# Revit family: 0043426
name_source: partatom
category: Lighting Fixtures
revit_build: Autodesk Revit 2017 (Build: 20190507_1515(x64)
units: mm (PartAtom-declared; Revit-internal decimal feet)

## family parameters
Cut with Voids When Loaded = No
Host = Face
Light Source = Yes
OmniClass Number = 23.80.70.00
OmniClass Title = Lighting
Part Type = Normal
Room Calculation Point = No
Round Connector Dimension = Use Diameter
Shared = No

## types (16) — shared parameters
Assembly Code = D5020200
AssetType = Fixed
ClassificationName = Uniclass2015
ClassificationValue = EF_70_80
Color Filter = 16777215
Default Elevation = 1219 mm
Dimming Lamp Color Temperature Shift = <None>
DocumentationLiterature = http://www.sylvania-lighting.com
ElectricShockClassification = Class I
Emit Shape Visible in Rendering = No
Emit from Circle Diameter = 610 mm
IfcExportAs = IfcLightFixtureType
IfcExportType = IfcLightFixtureType
ImpactProtectionIndex = IK03
IngressProtection = IP44
Keynote = 16500
Lamp = LED
LampColourRenderingIndex = 80
LampMacAdamStep = 6
LampsType = LED
Manufacturer = Feilo Sylvania
ManufacturerName = Feilo Sylvania
Material = steel housing, other diffuser
Material_1_SYL = <By Category>
Material_2_SYL = <By Category>
Material_3_SYL = <By Category>
Material_4_SYL = <By Category>
SENSOR_SYL = 12 mm  [stored 0.0393701 ft]
Tilt Angle = -90.00°
Type Image = <None>
URL = http://www.sylvania-lighting.com
Voltage = 0 V
YIN_SENSOR_SYL = No
zero-valued in all types: Cost

## per-type parameters (varying)
- 0043436_3000K START eco Surface IP44 2050LM MW 830/840 DT: Apparent Load=0 VA; BOTTOM_HEIGHT_SYL=85 mm  [stored 0.278871 ft]; BOTTOM_R_SYL=150 mm; LUM_H_SYL=100 mm  [stored 0.328084 ft]; LUM_R_HEIGHT_SYL=70 mm; LUM_R_SYL=180 mm  [stored 0.590551 ft]; LampColourTemperature=3000 K; LampNominalLuminous=2050 lm; Model=Start eco Surface IP44 2050lm MW 830/840 DualTone; ModelNumber=0043436; ModelReference=Start eco Surface IP44 2050lm MW 830/840 DualTone; Name=Start eco Surface IP44 2050lm MW 830/840 DualTone; NominalDepth=360 mm  [stored 1.1811 ft]; NominalHeight=100 mm  [stored 0.328084 ft]; NominalLength=360 mm  [stored 1.1811 ft]; Photometric Web File=0043436_3000K.ies; PowerFactor=0; TypeName=Start eco Surface IP44 2050lm MW 830/840 DualTone; Weight=3.42 kg; YIN_180_SYL=No; YIN_250_SYL=No; YIN_330_SYL=No; YIN_360_SYL=Yes
- 0043435_4000K START eco Surface IP44 1550LM MW 830/840 DT: Apparent Load=0 VA; BOTTOM_HEIGHT_SYL=81 mm  [stored 0.265748 ft]; BOTTOM_R_SYL=150 mm; LUM_H_SYL=96 mm  [stored 0.314961 ft]; LUM_R_HEIGHT_SYL=66 mm  [stored 0.216535 ft]; LUM_R_SYL=165 mm; LampColourTemperature=4000 K; LampNominalLuminous=1550 lm; Model=Start eco Surface IP44 1550lm MW 830/840 DualTone; ModelNumber=0043435; ModelReference=Start eco Surface IP44 1550lm MW 830/840 DualTone; Name=Start eco Surface IP44 1550lm MW 830/840 DualTone; NominalDepth=330 mm; NominalHeight=96 mm  [stored 0.314961 ft]; NominalLength=330 mm; Photometric Web File=0043435_4000K.ies; PowerFactor=0; TypeName=Start eco Surface IP44 1550lm MW 830/840 DualTone; Weight=3.42 kg; YIN_180_SYL=No; YIN_250_SYL=No; YIN_330_SYL=Yes; YIN_360_SYL=No
- 0043435_3000K START eco Surface IP44 1550LM MW 830/840 DT: Apparent Load=0 VA; BOTTOM_HEIGHT_SYL=81 mm  [stored 0.265748 ft]; BOTTOM_R_SYL=150 mm; LUM_H_SYL=96 mm  [stored 0.314961 ft]; LUM_R_HEIGHT_SYL=66 mm  [stored 0.216535 ft]; LUM_R_SYL=165 mm; LampColourTemperature=3000 K; LampNominalLuminous=1550 lm; Model=Start eco Surface IP44 1550lm MW 830/840 DualTone; ModelNumber=0043435; ModelReference=Start eco Surface IP44 1550lm MW 830/840 DualTone; Name=Start eco Surface IP44 1550lm MW 830/840 DualTone; NominalDepth=330 mm; NominalHeight=96 mm  [stored 0.314961 ft]; NominalLength=330 mm; Photometric Web File=0043435_3000K.ies; PowerFactor=0; TypeName=Start eco Surface IP44 1550lm MW 830/840 DualTone; Weight=3.42 kg; YIN_180_SYL=No; YIN_250_SYL=No; YIN_330_SYL=Yes; YIN_360_SYL=No
- 0043434_4000K START eco Surface IP44 2050LM DIM 30/840 DT: Apparent Load=0 VA; BOTTOM_HEIGHT_SYL=85 mm  [stored 0.278871 ft]; BOTTOM_R_SYL=150 mm; LUM_H_SYL=100 mm  [stored 0.328084 ft]; LUM_R_HEIGHT_SYL=70 mm; LUM_R_SYL=180 mm  [stored 0.590551 ft]; LampColourTemperature=4000 K; LampNominalLuminous=2050 lm; Model=Start eco Surface IP44 2050lm DIM 830/840 DualTone; ModelNumber=0043434; ModelReference=Start eco Surface IP44 2050lm DIM 830/840 DualTone; Name=Start eco Surface IP44 2050lm DIM 830/840 DualTone; NominalDepth=360 mm  [stored 1.1811 ft]; NominalHeight=100 mm  [stored 0.328084 ft]; NominalLength=360 mm  [stored 1.1811 ft]; Photometric Web File=0043434_4000K.ies; PowerFactor=0; TypeName=Start eco Surface IP44 2050lm DIM 830/840 DualTone; Weight=3.54 kg; YIN_180_SYL=No; YIN_250_SYL=No; YIN_330_SYL=No; YIN_360_SYL=Yes
- 0043434_3000K START eco Surface IP44 2050LM DIM 30/840 DT: Apparent Load=0 VA; BOTTOM_HEIGHT_SYL=85 mm  [stored 0.278871 ft]; BOTTOM_R_SYL=150 mm; LUM_H_SYL=100 mm  [stored 0.328084 ft]; LUM_R_HEIGHT_SYL=70 mm; LUM_R_SYL=180 mm  [stored 0.590551 ft]; LampColourTemperature=3000 K; LampNominalLuminous=2050 lm; Model=Start eco Surface IP44 2050lm DIM 830/840 DualTone; ModelNumber=0043434; ModelReference=Start eco Surface IP44 2050lm DIM 830/840 DualTone; Name=Start eco Surface IP44 2050lm DIM 830/840 DualTone; NominalDepth=360 mm  [stored 1.1811 ft]; NominalHeight=100 mm  [stored 0.328084 ft]; NominalLength=360 mm  [stored 1.1811 ft]; Photometric Web File=0043434_3000K.ies; PowerFactor=0; TypeName=Start eco Surface IP44 2050lm DIM 830/840 DualTone; Weight=3.54 kg; YIN_180_SYL=No; YIN_250_SYL=No; YIN_330_SYL=No; YIN_360_SYL=Yes
- 0043433_4000K START eco Surface IP44 1550LM DIM 830/840 DT: Apparent Load=0 VA; BOTTOM_HEIGHT_SYL=81 mm  [stored 0.265748 ft]; BOTTOM_R_SYL=150 mm; LUM_H_SYL=96 mm  [stored 0.314961 ft]; LUM_R_HEIGHT_SYL=66 mm  [stored 0.216535 ft]; LUM_R_SYL=165 mm; LampColourTemperature=4000 K; LampNominalLuminous=1550 lm; Model=Start eco Surface IP44 1550lm DIM 830/840 DualTone; ModelNumber=0043433; ModelReference=Start eco Surface IP44 1550lm DIM 830/840 DualTone; Name=Start eco Surface IP44 1550lm DIM 830/840 DualTone; NominalDepth=330 mm; NominalHeight=96 mm  [stored 0.314961 ft]; NominalLength=330 mm; Photometric Web File=0043433_4000K.ies; PowerFactor=0; TypeName=Start eco Surface IP44 1550lm DIM 830/840 DualTone; Weight=3.54 kg; YIN_180_SYL=No; YIN_250_SYL=No; YIN_330_SYL=Yes; YIN_360_SYL=No
- 0043433_3000K START eco Surface IP44 1550LM DIM 830/840 DT: Apparent Load=0 VA; BOTTOM_HEIGHT_SYL=81 mm  [stored 0.265748 ft]; BOTTOM_R_SYL=150 mm; LUM_H_SYL=96 mm  [stored 0.314961 ft]; LUM_R_HEIGHT_SYL=66 mm  [stored 0.216535 ft]; LUM_R_SYL=165 mm; LampColourTemperature=3000 K; LampNominalLuminous=1550 lm; Model=Start eco Surface IP44 1550lm DIM 830/840 DualTone; ModelNumber=0043433; ModelReference=Start eco Surface IP44 1550lm DIM 830/840 DualTone; Name=Start eco Surface IP44 1550lm DIM 830/840 DualTone; NominalDepth=330 mm; NominalHeight=96 mm  [stored 0.314961 ft]; NominalLength=330 mm; Photometric Web File=0043433_3000K.ies; PowerFactor=0; TypeName=Start eco Surface IP44 1550lm DIM 830/840 DualTone; Weight=3.54 kg; YIN_180_SYL=No; YIN_250_SYL=No; YIN_330_SYL=Yes; YIN_360_SYL=No
- 0043428_4000K START eco Surface IP44 2050LM 830/840 DT: Apparent Load=0 VA; BOTTOM_HEIGHT_SYL=85 mm  [stored 0.278871 ft]; BOTTOM_R_SYL=150 mm; LUM_H_SYL=100 mm  [stored 0.328084 ft]; LUM_R_HEIGHT_SYL=70 mm; LUM_R_SYL=180 mm  [stored 0.590551 ft]; LampColourTemperature=4000 K; LampNominalLuminous=2050 lm; Model=Start eco Surface IP44 2050lm 830/840 DualTone; ModelNumber=0043428; ModelReference=Start eco Surface IP44 2050lm 830/840 DualTone; Name=Start eco Surface IP44 2050lm 830/840 DualTone; NominalDepth=360 mm  [stored 1.1811 ft]; NominalHeight=100 mm  [stored 0.328084 ft]; NominalLength=360 mm  [stored 1.1811 ft]; Photometric Web File=0043428_4000K.ies; PowerFactor=0; TypeName=Start eco Surface IP44 2050lm 830/840 DualTone; Weight=3.12 kg; YIN_180_SYL=No; YIN_250_SYL=No; YIN_330_SYL=No; YIN_360_SYL=Yes
- 0043428_3000K START eco Surface IP44 2050LM 830/840 DT: Apparent Load=0 VA; BOTTOM_HEIGHT_SYL=85 mm  [stored 0.278871 ft]; BOTTOM_R_SYL=150 mm; LUM_H_SYL=100 mm  [stored 0.328084 ft]; LUM_R_HEIGHT_SYL=70 mm; LUM_R_SYL=180 mm  [stored 0.590551 ft]; LampColourTemperature=3000 K; LampNominalLuminous=2050 lm; Model=Start eco Surface IP44 2050lm 830/840 DualTone; ModelNumber=0043428; ModelReference=Start eco Surface IP44 2050lm 830/840 DualTone; Name=Start eco Surface IP44 2050lm 830/840 DualTone; NominalDepth=360 mm  [stored 1.1811 ft]; NominalHeight=100 mm  [stored 0.328084 ft]; NominalLength=360 mm  [stored 1.1811 ft]; Photometric Web File=0043428_3000K.ies; PowerFactor=0; TypeName=Start eco Surface IP44 2050lm 830/840 DualTone; Weight=3.12 kg; YIN_180_SYL=No; YIN_250_SYL=No; YIN_330_SYL=No; YIN_360_SYL=Yes
- 0043427_4000K START eco Surface IP44 1550LM 830/840 DT: Apparent Load=0 VA; BOTTOM_HEIGHT_SYL=81 mm  [stored 0.265748 ft]; BOTTOM_R_SYL=150 mm; LUM_H_SYL=96 mm  [stored 0.314961 ft]; LUM_R_HEIGHT_SYL=66 mm  [stored 0.216535 ft]; LUM_R_SYL=165 mm; LampColourTemperature=4000 K; LampNominalLuminous=1550 lm; Model=Start eco Surface IP44 1550lm 830/840 DualTone; ModelNumber=0043427; ModelReference=Start eco Surface IP44 1550lm 830/840 DualTone; Name=Start eco Surface IP44 1550lm 830/840 DualTone; NominalDepth=330 mm; NominalHeight=96 mm  [stored 0.314961 ft]; NominalLength=330 mm; Photometric Web File=0043427_4000K.ies; PowerFactor=0; TypeName=Start eco Surface IP44 1550lm 830/840 DualTone; Weight=3.12 kg; YIN_180_SYL=No; YIN_250_SYL=No; YIN_330_SYL=Yes; YIN_360_SYL=No
- 0043427_3000K START eco Surface IP44 1550LM 830/840 DT: Apparent Load=0 VA; BOTTOM_HEIGHT_SYL=81 mm  [stored 0.265748 ft]; BOTTOM_R_SYL=150 mm; LUM_H_SYL=96 mm  [stored 0.314961 ft]; LUM_R_HEIGHT_SYL=66 mm  [stored 0.216535 ft]; LUM_R_SYL=165 mm; LampColourTemperature=3000 K; LampNominalLuminous=1550 lm; Model=Start eco Surface IP44 1550lm 830/840 DualTone; ModelNumber=0043427; ModelReference=Start eco Surface IP44 1550lm 830/840 DualTone; Name=Start eco Surface IP44 1550lm 830/840 DualTone; NominalDepth=330 mm; NominalHeight=96 mm  [stored 0.314961 ft]; NominalLength=330 mm; Photometric Web File=0043427_3000K.ies; PowerFactor=0; TypeName=Start eco Surface IP44 1550lm 830/840 DualTone; Weight=3.12 kg; YIN_180_SYL=No; YIN_250_SYL=No; YIN_330_SYL=Yes; YIN_360_SYL=No
- 0043426_4000K START eco Surface IP44 1025LM 830/840 DT: Apparent Load=0 VA; BOTTOM_HEIGHT_SYL=65 mm  [stored 0.213255 ft]; BOTTOM_R_SYL=110 mm  [stored 0.360892 ft]; LUM_H_SYL=80 mm  [stored 0.262467 ft]; LUM_R_HEIGHT_SYL=50 mm  [stored 0.164042 ft]; LUM_R_SYL=125 mm  [stored 0.410105 ft]; LampColourTemperature=4000 K; LampNominalLuminous=1025 lm; Model=Start eco Surface IP44 1025lm 830/840 DualTone; ModelNumber=0043426; ModelReference=Start eco Surface IP44 1025lm 830/840 DualTone; Name=Start eco Surface IP44 1025lm 830/840 DualTone; NominalDepth=250 mm  [stored 0.82021 ft]; NominalHeight=80 mm  [stored 0.262467 ft]; NominalLength=250 mm  [stored 0.82021 ft]; Photometric Web File=0043426_4000K.ies; PowerFactor=0; TypeName=Start eco Surface IP44 1025lm 830/840 DualTone; Weight=1.5 kg; YIN_180_SYL=No; YIN_250_SYL=Yes; YIN_330_SYL=No; YIN_360_SYL=No
- 0043426_3000K START eco Surface IP44 1025LM 830/840 DT: Apparent Load=0 VA; BOTTOM_HEIGHT_SYL=65 mm  [stored 0.213255 ft]; BOTTOM_R_SYL=110 mm  [stored 0.360892 ft]; LUM_H_SYL=80 mm  [stored 0.262467 ft]; LUM_R_HEIGHT_SYL=50 mm  [stored 0.164042 ft]; LUM_R_SYL=125 mm  [stored 0.410105 ft]; LampColourTemperature=3000 K; LampNominalLuminous=1025 lm; Model=Start eco Surface IP44 1025lm 830/840 DualTone; ModelNumber=0043426; ModelReference=Start eco Surface IP44 1025lm 830/840 DualTone; Name=Start eco Surface IP44 1025lm 830/840 DualTone; NominalDepth=250 mm  [stored 0.82021 ft]; NominalHeight=80 mm  [stored 0.262467 ft]; NominalLength=250 mm  [stored 0.82021 ft]; Photometric Web File=0043426_3000K.ies; PowerFactor=0; TypeName=Start eco Surface IP44 1025lm 830/840 DualTone; Weight=1.5 kg; YIN_180_SYL=No; YIN_250_SYL=Yes; YIN_330_SYL=No; YIN_360_SYL=No
- 0043425_4000K START eco Surface IP44 520LM 830/840 DT: Apparent Load=6 VA; BOTTOM_HEIGHT_SYL=60 mm; BOTTOM_R_SYL=76 mm  [stored 0.249344 ft]; LUM_H_SYL=75 mm; LUM_R_HEIGHT_SYL=45 mm; LUM_R_SYL=90 mm  [stored 0.295276 ft]; LampColourTemperature=4000 K; LampNominalLuminous=520 lm; LuminousEfficacy=85 lm/W; Model=Start eco Surface IP44 520lm 830/840 DualTone; ModelNumber=0043425; ModelReference=Start eco Surface IP44 520lm 830/840 DualTone; Name=Start eco Surface IP44 520lm 830/840 DualTone; NominalDepth=180 mm  [stored 0.590551 ft]; NominalHeight=75 mm; NominalLength=180 mm  [stored 0.590551 ft]; Photometric Web File=0043425_4000K.ies; PowerConsumption=6 W; PowerFactor=0.8; TypeName=Start eco Surface IP44 520lm 830/840 DualTone; Weight=1.02 kg; YIN_180_SYL=Yes; YIN_250_SYL=No; YIN_330_SYL=No; YIN_360_SYL=No
- 0043425_3000K START eco Surface IP44 520LM 830/840 DT: Apparent Load=6 VA; BOTTOM_HEIGHT_SYL=60 mm; BOTTOM_R_SYL=76 mm  [stored 0.249344 ft]; LUM_H_SYL=75 mm; LUM_R_HEIGHT_SYL=45 mm; LUM_R_SYL=90 mm  [stored 0.295276 ft]; LampColourTemperature=3000 K; LampNominalLuminous=520 lm; LuminousEfficacy=85 lm/W; Model=Start eco Surface IP44 520lm 830/840 DualTone; ModelNumber=0043425; ModelReference=Start eco Surface IP44 520lm 830/840 DualTone; Name=Start eco Surface IP44 520lm 830/840 DualTone; NominalDepth=180 mm  [stored 0.590551 ft]; NominalHeight=75 mm; NominalLength=180 mm  [stored 0.590551 ft]; Photometric Web File=0043425_3000K.ies; PowerConsumption=6 W; PowerFactor=0.8; TypeName=Start eco Surface IP44 520lm 830/840 DualTone; Weight=1.02 kg; YIN_180_SYL=Yes; YIN_250_SYL=No; YIN_330_SYL=No; YIN_360_SYL=No
- 0043436_4000K START eco Surface IP44 2050LM MW 830/840 DT: Apparent Load=0 VA; BOTTOM_HEIGHT_SYL=85 mm  [stored 0.278871 ft]; BOTTOM_R_SYL=150 mm; LUM_H_SYL=100 mm  [stored 0.328084 ft]; LUM_R_HEIGHT_SYL=70 mm; LUM_R_SYL=180 mm  [stored 0.590551 ft]; LampColourTemperature=4000 K; LampNominalLuminous=2050 lm; Model=Start eco Surface IP44 2050lm MW 830/840 DualTone; ModelNumber=0043436; ModelReference=Start eco Surface IP44 2050lm MW 830/840 DualTone; Name=Start eco Surface IP44 2050lm MW 830/840 DualTone; NominalDepth=360 mm  [stored 1.1811 ft]; NominalHeight=100 mm  [stored 0.328084 ft]; NominalLength=360 mm  [stored 1.1811 ft]; Photometric Web File=0043436_4000K.ies; PowerFactor=0; TypeName=Start eco Surface IP44 2050lm MW 830/840 DualTone; Weight=3.42 kg; YIN_180_SYL=No; YIN_250_SYL=No; YIN_330_SYL=No; YIN_360_SYL=Yes

note: [stored X ft] marks values corroborated as IEEE doubles in the binary element streams (Revit-internal decimal feet)

## geometry (parser evidence)
native form markers: Sweep x1
no freeform markers — native parametric forms only
